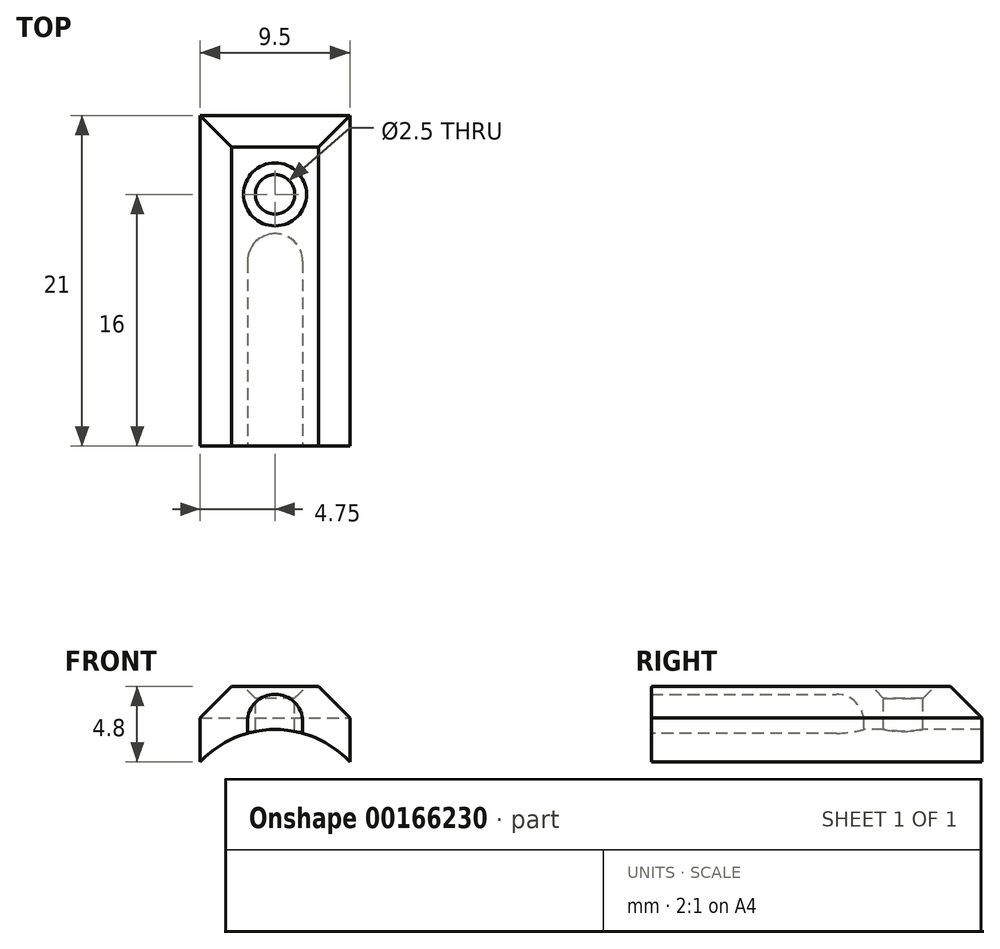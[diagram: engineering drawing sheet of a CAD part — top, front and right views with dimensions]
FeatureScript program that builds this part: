
annotation { "Feature Type Name" : "Feature", "Feature Type Description" : "" }
export const myFeature = defineFeature(function(context is Context, id is Id, definition is map)
    precondition{}
    {
        {
            assignVariable(context, id + "F0", {"name" : "Main_Length", "anyValue" : 21});
        }
        {
            assignVariable(context, id + "F1", {"name" : "Bore_Diam", "anyValue" : 3.5});
        }
        {
            assignVariable(context, id + "F2", {"name" : "Bore_Offset", "anyValue" : 0.5});
        }
        {
            assignVariable(context, id + "F3", {"name" : "Chamfer", "anyValue" : 2});
        }
        {
            assignVariable(context, id + "F4", {"name" : "Hole_Diam", "anyValue" : 2.5});
        }
        {
            var Q0;
            Q0=qCreatedBy(makeId("Front.planeOp"),FACE);
            var sketch = newSketch(context, id + "F5", { "sketchPlane" : qUnion([Q0])});
            skArc(sketch, "E0", {"start": v(4.75, 4.44) * mm, "mid": v(0, 6.5) * mm, "end": v(-4.75, 4.44) * mm});
            skLineSegment(sketch, "E1.bottom", {"start": v(4.75, 9.24) * mm, "end": v(-4.75, 9.24) * mm});
            skLineSegment(sketch, "E1.left", {"start": v(4.75, 9.24) * mm, "end": v(4.75, 4.44) * mm});
            skLineSegment(sketch, "E1.right", {"start": v(-4.75, 9.24) * mm, "end": v(-4.75, 4.44) * mm});
            skPoint(sketch, "E1.middle", {"position": v(0, 6.84) * mm});
            skArc(sketch, "E2", {"start": v(1.75, 6.99) * mm, "mid": v(0, 8.74) * mm, "end": v(-1.75, 6.99) * mm});
            skLineSegment(sketch, "E3", {"start": v(-1.75, 6.99) * mm, "end": v(-1.75, 6.26) * mm});
            skLineSegment(sketch, "E4", {"start": v(1.75, 6.99) * mm, "end": v(1.75, 6.26) * mm});
            skSolve(sketch);
        }
        {
            var Q0;
            Q0=makeQuery(id+"F5.imprint","IMPRINT",FACE,{"disambiguationData":[TD([[makeQuery(id+"F5.imprint","IMPRINT",EDGE,{"derivedFrom":sQuery(id+"F5.wireOp",EDGE,"E0")}),-1.0]])]});
            var Q1;
            {var subQ0=sQuery(id+"F5.wireOp",EDGE,"E2");var subQ1=sQuery(id+"F5.wireOp",EDGE,"E0");var subQ2=makeQuery(id+"F5.imprint","INTERSECT",VERTEX,{"disambiguationData":[OD(0.0)],"derivedFrom":[subQ1,subQ0]});Q1=makeQuery(id+"F5.imprint","IMPRINT",FACE,{"disambiguationData":[TD([[makeQuery(id+"F5.imprint","IMPRINT",EDGE,{"disambiguationData":[TD([[subQ2,-1.0]])],"derivedFrom":subQ1}),-1.0]])]});}
            var Q2;
            Q2=makeQuery(id+"F5.imprint","IMPRINT",FACE,{"disambiguationData":[TD([[makeQuery(id+"F5.imprint","IMPRINT",EDGE,{"derivedFrom":sQuery(id+"F5.wireOp",EDGE,"E2")}),1.0]])]});
            extrude(context, id + "F6", {"entities" : qUnion([Q0, Q1, Q2]), "oppositeDirection" : true, "depth" : (getVariable(context, 'Main_Length')) * mm});
        }
        {
            var Q0;
            Q0=makeQuery(id+"F6.opExtrude","SWEPT_EDGE",EDGE,{"disambiguationData":[OSD([sQuery(id+"F5.wireOp",EDGE,"E1.bottom"),sQuery(id+"F5.wireOp",EDGE,"E1.right")])]});
            var Q1;
            Q1=makeQuery(id+"F6.opExtrude","SWEPT_EDGE",EDGE,{"disambiguationData":[OSD([sQuery(id+"F5.wireOp",EDGE,"E1.bottom"),sQuery(id+"F5.wireOp",EDGE,"E1.left")])]});
            chamfer(context, id + "F7", {"entities" : qUnion([Q0, Q1]), "width" : (getVariable(context, 'Chamfer')) * mm, "tangentPropagation" : true});
        }
        {
            var Q0;
            Q0=makeQuery(id+"F6.opExtrude","CAP_EDGE",EDGE,{"disambiguationData":[OSD([sQuery(id+"F5.wireOp",EDGE,"E1.bottom")])],"isStart":false});
            chamfer(context, id + "F8", {"entities" : qUnion([Q0]), "width" : (getVariable(context, 'Chamfer')) * mm, "tangentPropagation" : true});
        }
        {
            var Q0;
            Q0=makeQuery(id+"F6.opExtrude","SWEPT_FACE",FACE,{"disambiguationData":[OSD([sQuery(id+"F5.wireOp",EDGE,"E1.bottom")])]});
            cPlane(context, id + "F9", {"entities" : qUnion([Q0]), "cplaneType" : CPlaneType.OFFSET, "offset" : (getVariable(context, 'Bore_Offset') + getVariable(context, 'Bore_Diam') / 2) * mm, "oppositeDirection" : true, "width" : 150 * mm, "height" : 150 * mm});
        }
        {
            var Q0;
            Q0=qCreatedBy(id+"F9.planeOp",FACE);
            var sketch = newSketch(context, id + "F10", { "sketchPlane" : qUnion([Q0])});
            skLineSegment(sketch, "E5", {"start": v(-1.75, 0) * mm, "end": v(-1.75, 11.75) * mm});
            skLineSegment(sketch, "E6", {"start": v(1.75, 0) * mm, "end": v(1.75, 11.75) * mm});
            skArc(sketch, "E7", {"start": v(1.75, 11.75) * mm, "mid": v(0, 13.5) * mm, "end": v(-1.75, 11.75) * mm});
            skLineSegment(sketch, "E8", {"start": v(-1.75, 0) * mm, "end": v(1.75, 0) * mm});
            skLineSegment(sketch, "E9", {"start": v(0, 0) * mm, "end": v(0, 13.5) * mm});
            skSolve(sketch);
        }
        {
            var Q0;
            {var subQ0=sQuery(id+"F10.wireOp",EDGE,"E5");Q0=makeQuery(id+"F10.imprint","IMPRINT",FACE,{"disambiguationData":[TD([[makeQuery(id+"F10.imprint","IMPRINT",EDGE,{"derivedFrom":subQ0}),-1.0]])]});}
            var Q1;
            Q1=sQuery(id+"F10.wireOp",EDGE,"E9");
            revolve(context, id + "F11", {"operationType" : NewBodyOperationType.REMOVE, "entities" : qUnion([Q0]), "axis" : qUnion([Q1]), "revolveType" : RevolveType.FULL, "oppositeDirection" : true});
        }
        {
            var Q0;
            {var subQ0=sQuery(id+"F10.wireOp",EDGE,"E6");Q0=makeQuery(id+"F10.imprint","IMPRINT",FACE,{"disambiguationData":[TD([[makeQuery(id+"F10.imprint","IMPRINT",EDGE,{"derivedFrom":subQ0}),1.0]])]});}
            var Q1;
            {var subQ0=sQuery(id+"F10.wireOp",EDGE,"E5");Q1=makeQuery(id+"F10.imprint","IMPRINT",FACE,{"disambiguationData":[TD([[makeQuery(id+"F10.imprint","IMPRINT",EDGE,{"derivedFrom":subQ0}),-1.0]])]});}
            extrude(context, id + "F12", {"entities" : qUnion([Q0, Q1]), "operationType" : NewBodyOperationType.REMOVE, "endBound" : BoundingType.THROUGH_ALL, "oppositeDirection" : true, "depth" : 25 * mm});
        }
        {
            var Q0;
            Q0=makeQuery(id+"F6.opExtrude","SWEPT_FACE",FACE,{"disambiguationData":[OSD([sQuery(id+"F5.wireOp",EDGE,"E1.bottom")])]});
            var sketch = newSketch(context, id + "F13", { "sketchPlane" : qUnion([Q0])});
            skCircle(sketch, "E10", {"center": v(0, 16) * mm, "radius": 1.25 * mm});
            skSolve(sketch);
        }
        {
            var Q0;
            Q0=sQuery(id+"F13.wireOp",VERTEX,"E10.center");
            var Q1;
            Q1=makeQuery(id+"F6.opExtrude","SWEPT_BODY",BODY,{"disambiguationData":[OSD([sQuery(id+"F5.wireOp",EDGE,"E0"),sQuery(id+"F5.wireOp",EDGE,"E1.bottom"),sQuery(id+"F5.wireOp",EDGE,"E1.left"),sQuery(id+"F5.wireOp",EDGE,"E1.right")])]});
            hole(context, id + "F14", {"style" : HoleStyle.C_SINK, "endStyle" : HoleEndStyle.THROUGH, "holeDiameter" : (getVariable(context, 'Hole_Diam')) * mm, "cSinkDiameter" : 4 * mm, "cSinkAngle" : 90 * degree, "locations" : qUnion([Q0]), "scope" : qUnion([Q1]), "isTappedThrough" : true});
        }
    });
